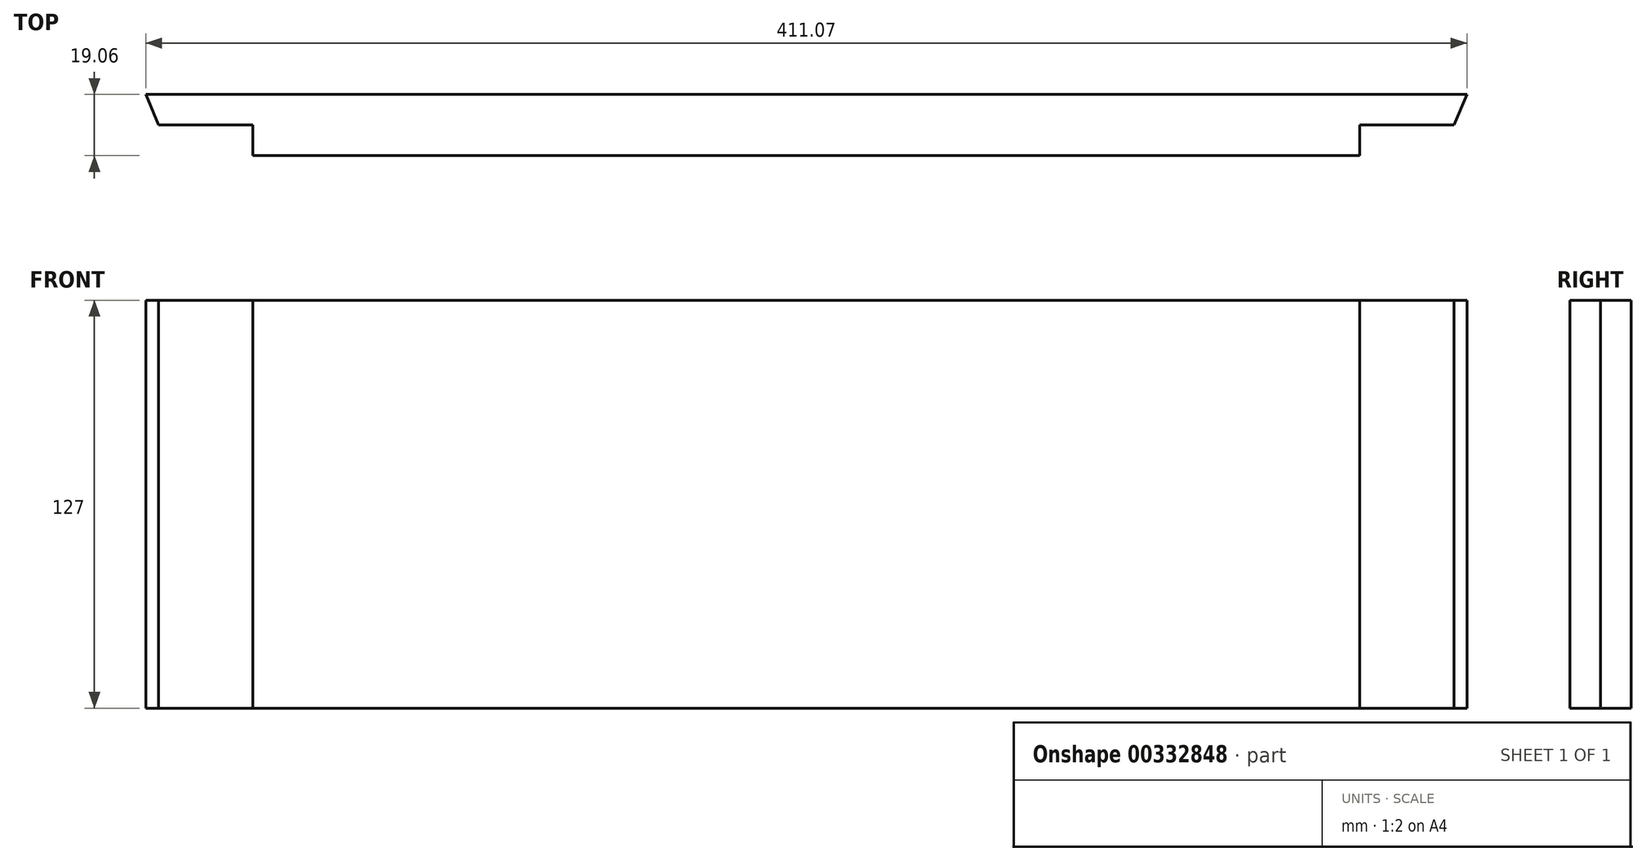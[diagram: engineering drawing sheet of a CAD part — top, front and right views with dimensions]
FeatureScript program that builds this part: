
annotation { "Feature Type Name" : "Feature", "Feature Type Description" : "" }
export const myFeature = defineFeature(function(context is Context, id is Id, definition is map)
    precondition{}
    {
        {
            var Q0;
            Q0=qCreatedBy(makeId("Top.planeOp"),FACE);
            var sketch = newSketch(context, id + "F0", { "sketchPlane" : qUnion([Q0])});
            skLineSegment(sketch, "E0", {"start": v(25.4, -9.53) * mm, "end": v(369.89, -9.53) * mm});
            skLineSegment(sketch, "E1", {"start": v(399.23, 0) * mm, "end": v(403.18, 9.52) * mm});
            skLineSegment(sketch, "E2", {"start": v(403.18, 9.52) * mm, "end": v(-7.9, 9.53) * mm});
            skLineSegment(sketch, "E3", {"start": v(-7.9, 9.53) * mm, "end": v(-3.95, 0) * mm});
            skLineSegment(sketch, "E4.top", {"start": v(369.89, 0) * mm, "end": v(399.23, 0) * mm});
            skLineSegment(sketch, "E4.left", {"start": v(369.89, -9.53) * mm, "end": v(369.89, 0) * mm});
            skPoint(sketch, "E5.orphan", {"position": v(395.29, -9.53) * mm});
            skLineSegment(sketch, "E6.top", {"start": v(25.4, 0) * mm, "end": v(-3.95, 0) * mm});
            skLineSegment(sketch, "E6.left", {"start": v(25.4, -9.53) * mm, "end": v(25.4, 0) * mm});
            skPoint(sketch, "E7.orphan", {"position": v(0, -9.53) * mm});
            skSolve(sketch);
        }
        {
            var Q0;
            Q0=makeQuery(id+"F0.imprint","IMPRINT",FACE,{"disambiguationData":[TD([[makeQuery(id+"F0.imprint","IMPRINT",EDGE,{"derivedFrom":sQuery(id+"F0.wireOp",EDGE,"E0")}),1.0]])]});
            extrude(context, id + "F1", {"entities" : qUnion([Q0]), "endBound" : BoundingType.SYMMETRIC, "depth" : 127 * mm});
        }
    });
